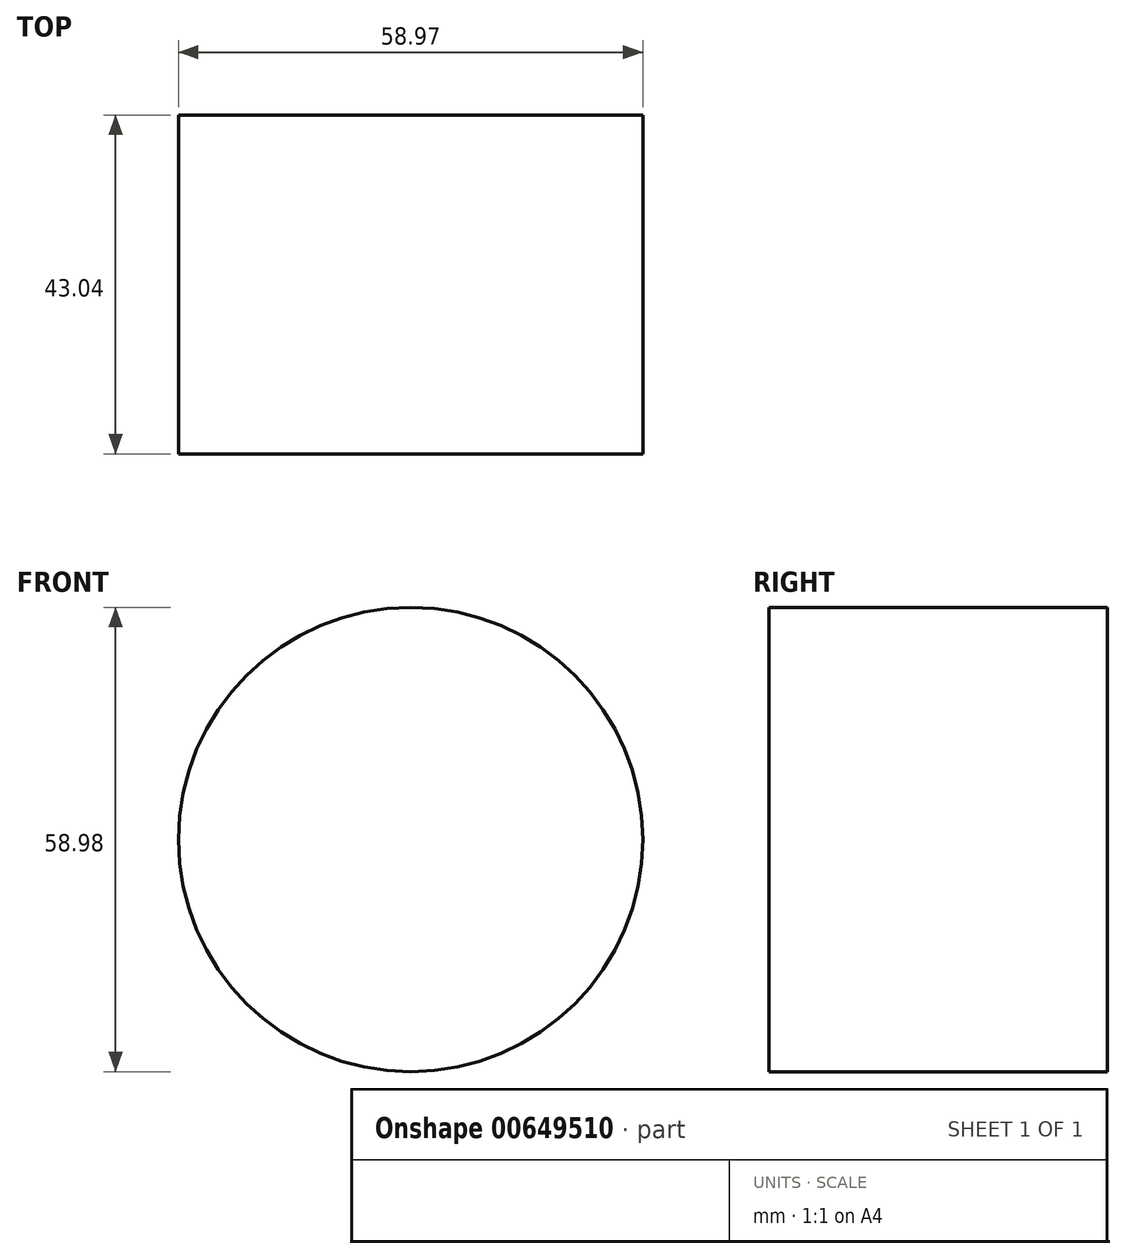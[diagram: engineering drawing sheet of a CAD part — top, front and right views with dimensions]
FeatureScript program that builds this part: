
annotation { "Feature Type Name" : "Feature", "Feature Type Description" : "" }
export const myFeature = defineFeature(function(context is Context, id is Id, definition is map)
    precondition{}
    {
        {
            var Q0;
            Q0=qCreatedBy(makeId("Top.planeOp"),FACE);
            var sketch = newSketch(context, id + "F0", { "sketchPlane" : qUnion([Q0])});
            skLineSegment(sketch, "E0.bottom", {"start": v(-48.21, 57.46) * mm, "end": v(-18.73, 57.46) * mm});
            skLineSegment(sketch, "E0.top", {"start": v(-48.21, 14.42) * mm, "end": v(-18.73, 14.42) * mm});
            skLineSegment(sketch, "E0.left", {"start": v(-48.21, 57.46) * mm, "end": v(-48.21, 14.42) * mm});
            skLineSegment(sketch, "E0.right", {"start": v(-18.73, 57.46) * mm, "end": v(-18.73, 14.42) * mm});
            skSolve(sketch);
        }
        {
            var Q0;
            Q0=makeQuery(id+"F0.imprint","IMPRINT",FACE,{"disambiguationData":[TD([[makeQuery(id+"F0.imprint","IMPRINT",EDGE,{"derivedFrom":sQuery(id+"F0.wireOp",EDGE,"E0.bottom")}),-1.0]])]});
            var Q1;
            Q1=sQuery(id+"F0.wireOp",EDGE,"E0.right");
            revolve(context, id + "F1", {"entities" : qUnion([Q0]), "axis" : qUnion([Q1]), "revolveType" : RevolveType.FULL});
        }
    });
